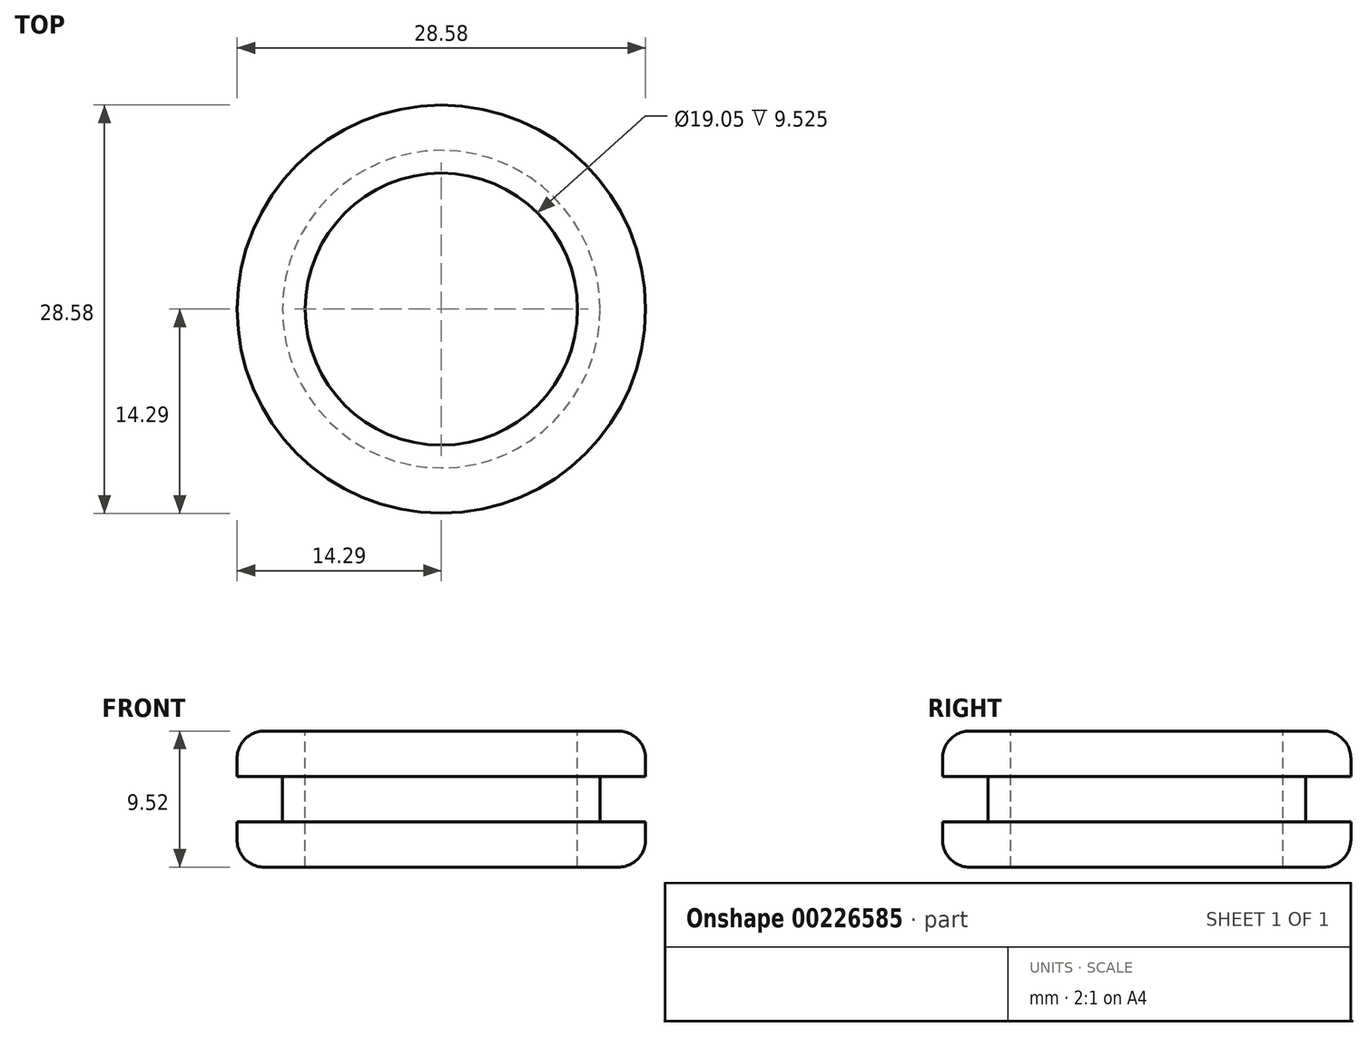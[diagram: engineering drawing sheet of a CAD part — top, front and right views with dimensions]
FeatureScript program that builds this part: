
annotation { "Feature Type Name" : "Feature", "Feature Type Description" : "" }
export const myFeature = defineFeature(function(context is Context, id is Id, definition is map)
    precondition{}
    {
        {
            var Q0;
            Q0=qCreatedBy(makeId("Front.planeOp"),FACE);
            var sketch = newSketch(context, id + "F0", { "sketchPlane" : qUnion([Q0])});
            skLineSegment(sketch, "E0", {"start": v(0, 17.62) * mm, "end": v(0, -18.14) * mm, "construction": true});
            skLineSegment(sketch, "E1", {"start": v(-12.38, 4.76) * mm, "end": v(12.38, 4.76) * mm});
            skLineSegment(sketch, "E2", {"start": v(-14.29, 2.86) * mm, "end": v(-14.29, 1.59) * mm});
            skLineSegment(sketch, "E3", {"start": v(14.29, 2.86) * mm, "end": v(14.29, 1.59) * mm});
            skLineSegment(sketch, "E4", {"start": v(-12.38, -4.76) * mm, "end": v(12.38, -4.76) * mm});
            skLineSegment(sketch, "E5", {"start": v(-14.29, -1.59) * mm, "end": v(-14.29, -2.86) * mm});
            skLineSegment(sketch, "E6", {"start": v(14.29, -1.59) * mm, "end": v(14.29, -2.86) * mm});
            skLineSegment(sketch, "E7", {"start": v(-14.29, 1.59) * mm, "end": v(-11.11, 1.59) * mm});
            skLineSegment(sketch, "E8", {"start": v(11.11, 1.59) * mm, "end": v(14.29, 1.59) * mm});
            skLineSegment(sketch, "E9", {"start": v(-14.29, -1.59) * mm, "end": v(-11.11, -1.59) * mm});
            skLineSegment(sketch, "E10", {"start": v(11.11, -1.59) * mm, "end": v(14.29, -1.59) * mm});
            skLineSegment(sketch, "E11", {"start": v(11.11, 1.59) * mm, "end": v(11.11, -1.59) * mm});
            skLineSegment(sketch, "E12", {"start": v(-11.11, 1.59) * mm, "end": v(-11.11, -1.59) * mm});
            skArc(sketch, "E13", {"start": v(-14.29, 2.86) * mm, "mid": v(-13.73, 4.2) * mm, "end": v(-12.38, 4.76) * mm});
            skArc(sketch, "E14.MirrorCS", {"start": v(14.29, 2.86) * mm, "mid": v(13.73, 4.2) * mm, "end": v(12.38, 4.76) * mm});
            skArc(sketch, "E15.MirrorCS", {"start": v(14.29, -2.86) * mm, "mid": v(13.73, -4.2) * mm, "end": v(12.38, -4.76) * mm});
            skArc(sketch, "E16.MirrorCS", {"start": v(-14.29, -2.86) * mm, "mid": v(-13.73, -4.2) * mm, "end": v(-12.38, -4.76) * mm});
            skLineSegment(sketch, "E17", {"start": v(-9.53, 4.76) * mm, "end": v(-9.53, -4.76) * mm});
            skLineSegment(sketch, "E18", {"start": v(9.53, 4.76) * mm, "end": v(9.53, -4.76) * mm});
            skSolve(sketch);
        }
        {
            var Q0;
            Q0=makeQuery(id+"F0.imprint","IMPRINT",FACE,{"disambiguationData":[TD([[makeQuery(id+"F0.imprint","IMPRINT",EDGE,{"derivedFrom":sQuery(id+"F0.wireOp",EDGE,"E2")}),1.0]])]});
            var Q1;
            Q1=sQuery(id+"F0.wireOp",EDGE,"E0");
            revolve(context, id + "F1", {"entities" : qUnion([Q0]), "axis" : qUnion([Q1]), "revolveType" : RevolveType.FULL});
        }
    });
